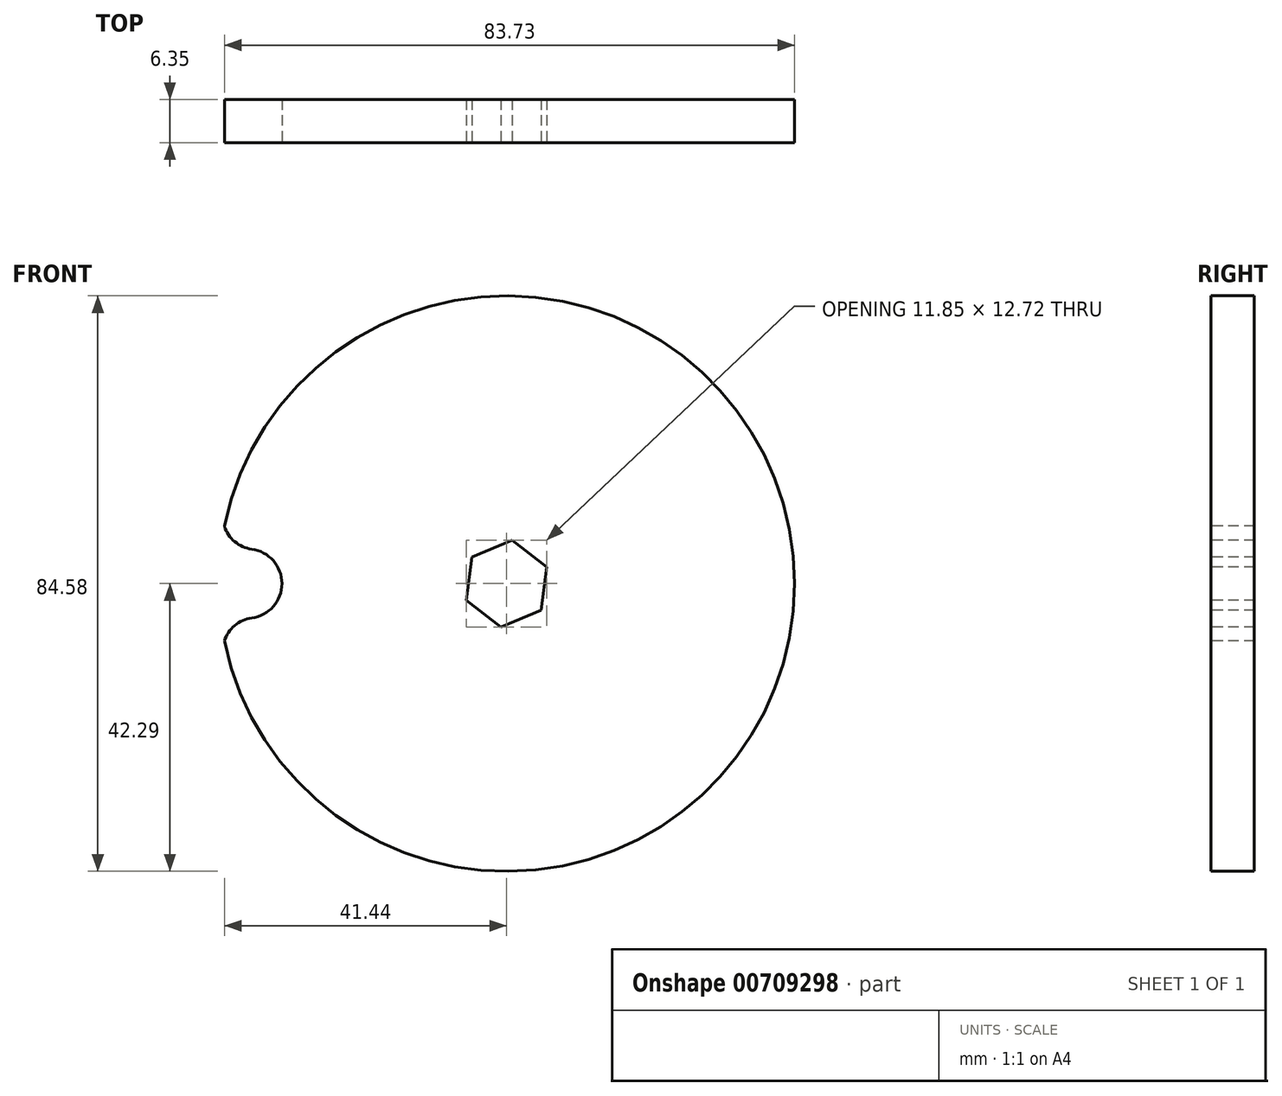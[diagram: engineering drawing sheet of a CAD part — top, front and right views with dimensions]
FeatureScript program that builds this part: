
annotation { "Feature Type Name" : "Feature", "Feature Type Description" : "" }
export const myFeature = defineFeature(function(context is Context, id is Id, definition is map)
    precondition{}
    {
        {
            var Q0;
            Q0=qCreatedBy(makeId("Front.planeOp"),FACE);
            var sketch = newSketch(context, id + "F0", { "sketchPlane" : qUnion([Q0])});
            skLineSegment(sketch, "E0", {"start": v(0, 0) * mm, "end": v(-76.2, 0) * mm, "construction": true});
            skCircle(sketch, "E1", {"center": v(-76.2, 0) * mm, "radius": 38.1 * mm, "construction": true});
            skCircle(sketch, "E2", {"center": v(0, 0) * mm, "radius": 38.1 * mm, "construction": true});
            skCircle(sketch, "E3", {"center": v(-38.1, 0) * mm, "radius": 4.98 * mm, "construction": true});
            skCircle(sketch, "E4", {"center": v(-36.8, 9.88) * mm, "radius": 4.98 * mm, "construction": true});
            skLineSegment(sketch, "E5", {"start": v(0, 0) * mm, "end": v(-37.77, 4.97) * mm, "construction": true});
            skCircle(sketch, "E6", {"center": v(0, 0) * mm, "radius": 42.29 * mm});
            skPoint(sketch, "E7", {"position": v(-42.29, 0) * mm});
            skPoint(sketch, "E8", {"position": v(-43.08, 0) * mm});
            skLineSegment(sketch, "E9", {"start": v(0, 0) * mm, "end": v(-36.8, 9.88) * mm, "construction": true});
            skSolve(sketch);
        }
        {
            var Q0;
            Q0 = qSketchRegion(id + "F0", true);
            extrude(context, id + "F1", {"entities" : qUnion([Q0]), "oppositeDirection" : true, "depth" : 6.35 * mm, "offsetDistance" : 25.4 * mm});
        }
        {
            var Q0;
            Q0=makeQuery(id+"F0.imprint","IMPRINT",FACE,{"disambiguationData":[TD([[makeQuery(id+"F0.imprint","IMPRINT",EDGE,{"derivedFrom":sQuery(id+"F0.wireOp",EDGE,"E6")}),1.0]])]});
            var sketch = newSketch(context, id + "F2", { "sketchPlane" : qUnion([Q0])});
            skArc(sketch, "E10", {"start": v(-37.43, -5.07) * mm, "mid": v(-32.99, 0) * mm, "end": v(-37.43, 5.07) * mm});
            skArc(sketch, "E11", {"start": v(-41.44, 8.45) * mm, "mid": v(-39.93, 6.17) * mm, "end": v(-37.43, 5.07) * mm});
            skLineSegment(sketch, "E12", {"start": v(0, 0) * mm, "end": v(-37.76, -5.11) * mm, "construction": true});
            skArc(sketch, "E13", {"start": v(-37.42, -5.07) * mm, "mid": v(-39.93, -6.17) * mm, "end": v(-41.44, -8.45) * mm});
            skArc(sketch, "E14", {"start": v(-41.44, 8.45) * mm, "mid": v(-42.29, 0) * mm, "end": v(-41.44, -8.45) * mm});
            skSolve(sketch);
        }
        {
            var Q0;
            Q0 = qSketchRegion(id + "F2", true);
            extrude(context, id + "F3", {"entities" : qUnion([Q0]), "operationType" : NewBodyOperationType.REMOVE, "endBound" : BoundingType.THROUGH_ALL, "oppositeDirection" : true, "depth" : 25.4 * mm, "offsetDistance" : 25.4 * mm});
        }
        {
            var Q0;
            Q0=makeQuery(id+"F0.imprint","IMPRINT",FACE,{"disambiguationData":[TD([[makeQuery(id+"F0.imprint","IMPRINT",EDGE,{"derivedFrom":sQuery(id+"F0.wireOp",EDGE,"E6")}),1.0]])]});
            var sketch = newSketch(context, id + "F4", { "sketchPlane" : qUnion([Q0])});
            skCircle(sketch, "E15", {"center": v(0, 0) * mm, "radius": 6.38 * mm, "construction": true});
            skCircle(sketch, "E16.cCircle", {"center": v(0, 0) * mm, "radius": 5.56 * mm, "construction": true});
            skLineSegment(sketch, "E16.0", {"start": v(-5.1, 3.9) * mm, "end": v(0.84, 6.36) * mm});
            skLineSegment(sketch, "E16.1", {"start": v(0.84, 6.36) * mm, "end": v(5.93, 2.46) * mm});
            skLineSegment(sketch, "E16.2", {"start": v(5.93, 2.46) * mm, "end": v(5.1, -3.9) * mm});
            skLineSegment(sketch, "E16.3", {"start": v(5.1, -3.9) * mm, "end": v(-0.84, -6.36) * mm});
            skLineSegment(sketch, "E16.4", {"start": v(-0.84, -6.36) * mm, "end": v(-5.93, -2.46) * mm});
            skLineSegment(sketch, "E16.5", {"start": v(-5.93, -2.46) * mm, "end": v(-5.1, 3.9) * mm});
            skPoint(sketch, "E16.0.midPoint", {"position": v(-2.13, 5.13) * mm});
            skSolve(sketch);
        }
        {
            var Q0;
            Q0 = qSketchRegion(id + "F4", true);
            extrude(context, id + "F5", {"entities" : qUnion([Q0]), "operationType" : NewBodyOperationType.REMOVE, "endBound" : BoundingType.THROUGH_ALL, "oppositeDirection" : true, "depth" : 25.4 * mm, "offsetDistance" : 25.4 * mm});
        }
    });
